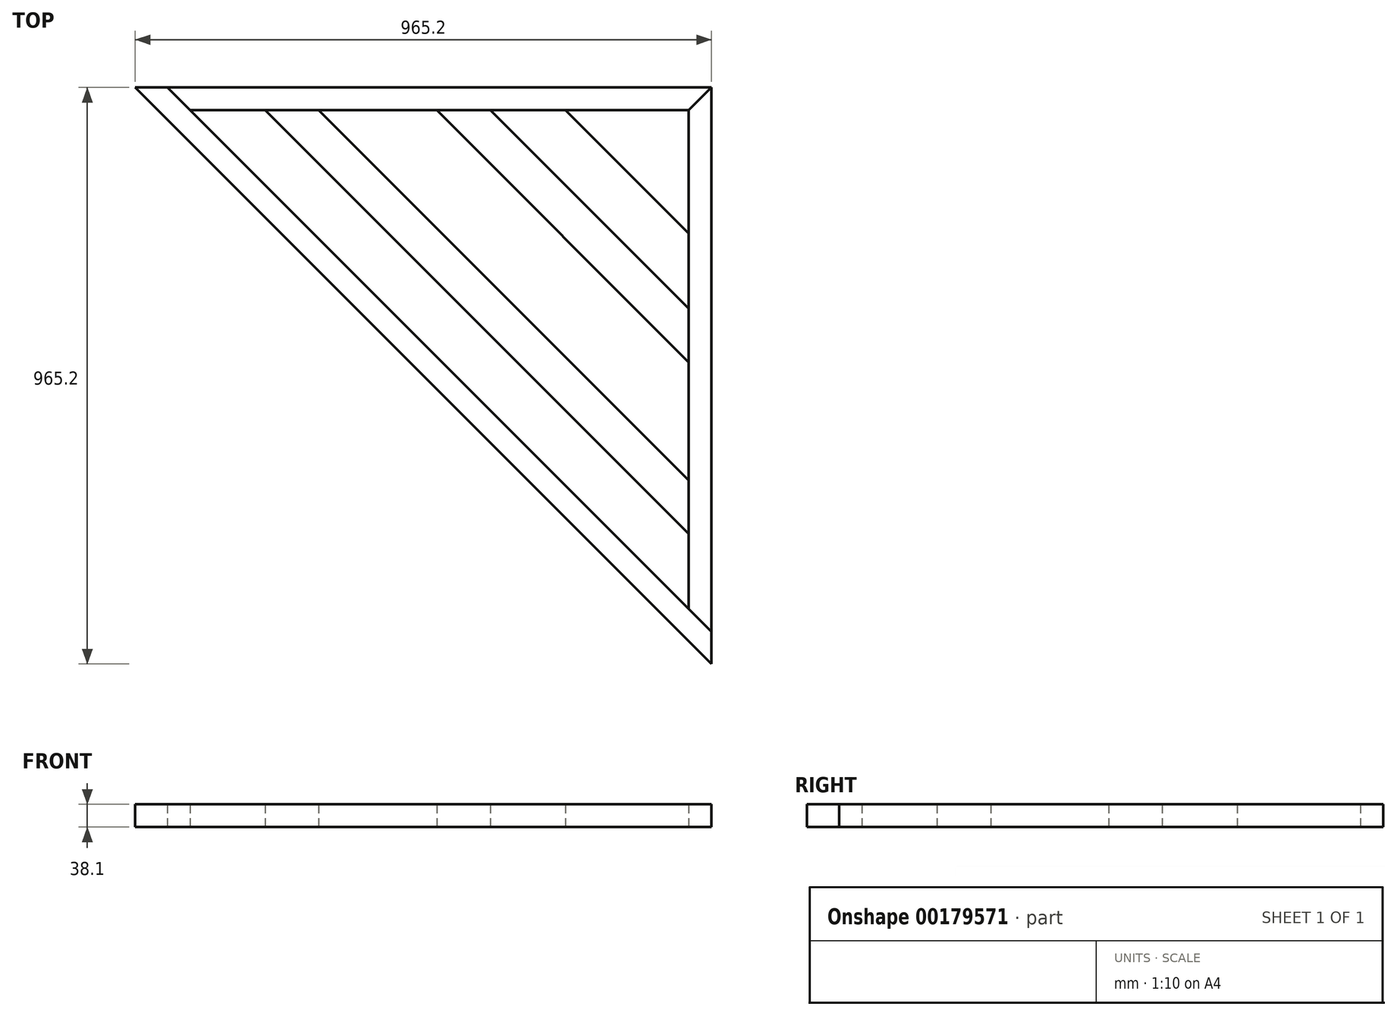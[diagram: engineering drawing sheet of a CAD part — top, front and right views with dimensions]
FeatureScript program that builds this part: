
annotation { "Feature Type Name" : "Feature", "Feature Type Description" : "" }
export const myFeature = defineFeature(function(context is Context, id is Id, definition is map)
    precondition{}
    {
        {
            var Q0;
            Q0=qCreatedBy(makeId("Top.planeOp"),FACE);
            var sketch = newSketch(context, id + "F0", { "sketchPlane" : qUnion([Q0])});
            skLineSegment(sketch, "E0", {"start": v(0, 0) * mm, "end": v(0, -835.12) * mm});
            skLineSegment(sketch, "E1", {"start": v(0, -889) * mm, "end": v(-927.1, 38.1) * mm});
            skLineSegment(sketch, "E2", {"start": v(-835.12, 0) * mm, "end": v(0, 0) * mm});
            skLineSegment(sketch, "E3", {"start": v(-873.22, 38.1) * mm, "end": v(38.1, -873.22) * mm});
            skLineSegment(sketch, "E4", {"start": v(-709.4, 0) * mm, "end": v(0, -709.4) * mm});
            skLineSegment(sketch, "E5", {"start": v(-619.6, 0) * mm, "end": v(0, -619.6) * mm});
            skLineSegment(sketch, "E6", {"start": v(-422.03, 0) * mm, "end": v(0, -422.03) * mm});
            skLineSegment(sketch, "E7", {"start": v(-332.22, 0) * mm, "end": v(0, -332.22) * mm});
            skLineSegment(sketch, "E8", {"start": v(-206.5, 0) * mm, "end": v(0, -206.5) * mm});
            skLineSegment(sketch, "E9", {"start": v(0, 0) * mm, "end": v(38.1, 38.1) * mm});
            skLineSegment(sketch, "E10", {"start": v(38.1, 38.1) * mm, "end": v(38.1, -927.1) * mm});
            skLineSegment(sketch, "E11", {"start": v(38.1, -927.1) * mm, "end": v(0, -889) * mm});
            skLineSegment(sketch, "E12", {"start": v(-927.1, 38.1) * mm, "end": v(38.1, 38.1) * mm});
            skSolve(sketch);
        }
        {
            var Q0;
            {var subQ6=sQuery(id+"F0.wireOp",EDGE,"E1");Q0=makeQuery(id+"F0.imprint","IMPRINT",FACE,{"disambiguationData":[TD([[makeQuery(id+"F0.imprint","IMPRINT",EDGE,{"derivedFrom":subQ6}),-1.0]])]});}
            var Q1;
            {var subQ0=sQuery(id+"F0.wireOp",EDGE,"E4");Q1=makeQuery(id+"F0.imprint","IMPRINT",FACE,{"disambiguationData":[TD([[makeQuery(id+"F0.imprint","IMPRINT",EDGE,{"derivedFrom":subQ0}),1.0]])]});}
            var Q2;
            {var subQ0=sQuery(id+"F0.wireOp",EDGE,"E6");Q2=makeQuery(id+"F0.imprint","IMPRINT",FACE,{"disambiguationData":[TD([[makeQuery(id+"F0.imprint","IMPRINT",EDGE,{"derivedFrom":subQ0}),1.0]])]});}
            var Q3;
            {var subQ3=sQuery(id+"F0.wireOp",EDGE,"E8");Q3=makeQuery(id+"F0.imprint","IMPRINT",FACE,{"disambiguationData":[TD([[makeQuery(id+"F0.imprint","IMPRINT",EDGE,{"derivedFrom":subQ3}),1.0]])]});}
            extrude(context, id + "F1", {"entities" : qUnion([Q0, Q1, Q2, Q3]), "depth" : 38.1 * mm});
        }
        {
            var Q0;
            {var subQ3=sQuery(id+"F0.wireOp",EDGE,"E4");Q0=makeQuery(id+"F0.imprint","IMPRINT",FACE,{"disambiguationData":[TD([[makeQuery(id+"F0.imprint","IMPRINT",EDGE,{"derivedFrom":subQ3}),-1.0]])]});}
            var Q1;
            {var subQ0=sQuery(id+"F0.wireOp",EDGE,"E5");Q1=makeQuery(id+"F0.imprint","IMPRINT",FACE,{"disambiguationData":[TD([[makeQuery(id+"F0.imprint","IMPRINT",EDGE,{"derivedFrom":subQ0}),1.0]])]});}
            var Q2;
            {var subQ0=sQuery(id+"F0.wireOp",EDGE,"E7");Q2=makeQuery(id+"F0.imprint","IMPRINT",FACE,{"disambiguationData":[TD([[makeQuery(id+"F0.imprint","IMPRINT",EDGE,{"derivedFrom":subQ0}),1.0]])]});}
            extrude(context, id + "F2", {"entities" : qUnion([Q0, Q1, Q2]), "depth" : 38.1 * mm});
        }
        {
            var Q0;
            {var subQ5=sQuery(id+"F0.wireOp",EDGE,"E9");Q0=makeQuery(id+"F0.imprint","IMPRINT",FACE,{"disambiguationData":[TD([[makeQuery(id+"F0.imprint","IMPRINT",EDGE,{"derivedFrom":subQ5}),1.0]])]});}
            extrude(context, id + "F3", {"entities" : qUnion([Q0]), "depth" : 38.1 * mm});
        }
        {
            var Q0;
            {var subQ7=sQuery(id+"F0.wireOp",EDGE,"E9");Q0=makeQuery(id+"F0.imprint","IMPRINT",FACE,{"disambiguationData":[TD([[makeQuery(id+"F0.imprint","IMPRINT",EDGE,{"derivedFrom":subQ7}),-1.0]])]});}
            extrude(context, id + "F4", {"entities" : qUnion([Q0]), "depth" : 38.1 * mm});
        }
    });
